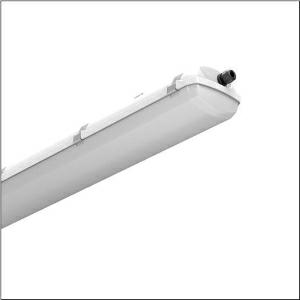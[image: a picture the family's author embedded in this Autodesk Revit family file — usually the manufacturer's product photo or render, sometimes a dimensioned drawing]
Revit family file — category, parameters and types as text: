
# Revit family: monsun_r__ex_51fxa27l440a_d3da
name_source: partatom
category: Lighting Fixtures
units: mm (PartAtom-declared; Revit-internal decimal feet)

## family parameters
Cut with Voids When Loaded = No
Host = Face
Light Source = No
Part Type = Normal
Room Calculation Point = No
Round Connector Dimension = Use Diameter
Shared = No

## types (1)
- Monsun® Ex (1 x LED, 4650 lm, 33 W, 4000K)
    Apparent Load = 33 VA
    CIE Flux Codes = 46 76 94 98 100
    Color Rendering = 80
    Color Temperature = 4000K
    Default Elevation = 1800 mm
    Description = Monsun® Ex, damp-proof luminaire, primary optical cover: cover, of PC, UV-stabilised, opal, light emission: direct distribution, primary light characteristic: symmetric, installation type: surface-mounted, LED, rated luminous flux: 4.650lm, luminous efficacy: 141lm/W, light colour: 840, colour temperature: 4000K, control gear: ON/OFF, with terminal, 3-pole, max. 2.5mm², through-wiring: 5x 2.5mm², mains connection: 220..250V, AC, 50/60Hz, rated input power: 33W, housing, of PC, light grey (RAL 7035), incl. 1x Ex cable gland M20 for cable diameter 7..12mm with sealing, incl. 1x Ex locking screw M20 with sealing, length: 1.280mm, width: 155mm, height: 105mm, clip for enclosure, of stainless steel, protection rating (complete): IP66, insulation class (complete): insulation class I (protective earthing), certification: CE, explosion class: zone 1,21 II 2G Ex eb mb op is IIC T4 Gb, II 2D Ex tb op is IIIC T67°C Db, impact resistance: IK10, permissible operating ambient temperature: -20..+40°C, contact your sales advisor before using the luminaires in applications with unclear chemical exposure, large temperature fluctuations or condensation-forming humidity, packaging unit: 1 piece
    Height = 105 mm
    Lamp = 1 x LED
    Lamp Light Flux = 4650 lm
    Lamp Power = 33 W
    Lamp count = 1
    Length = 1280 mm
    Luminous efficacy = 141 lm/W
    Manufacturer = Siteco
    ModVariant = No
    Model = 51FXA27L440A
    Mounting Place = Ceiling
    Mounting Type = Surface mounted
    Number of Poles = 1
    OnlyDefault = Yes
    Power Factor = 1
    Product Name = Monsun® Ex
    Product group = damp-proof luminaire
    ProductGroupID = 300
    Protection Class = Protection class I
    Protection Degree = IP 66
    RLX_Detail_Level = 1
    RLX_Emergency_Light_Flux = 0 lm
    RLX_Emergency_Type = 0
    RLX_Emergency_Type_DB = No
    RlxData = <blob elided: 41645 chars, md5=8d4e9882>
    Socket = socket
    Standby Power = 0 W
    System Light Flux = 4650 lm
    System Power = 33 W
    Type Comments = Product without accessories
    Type Image = l_1258882.jpg
    URL = http://relux.com
    VarID = ---
    Voltage = 0 V
    Weight = 0.00 kg
    Width = 155 mm

## geometry (parser evidence)
native form markers: Blend x4, Sweep x9
no freeform markers — native parametric forms only
